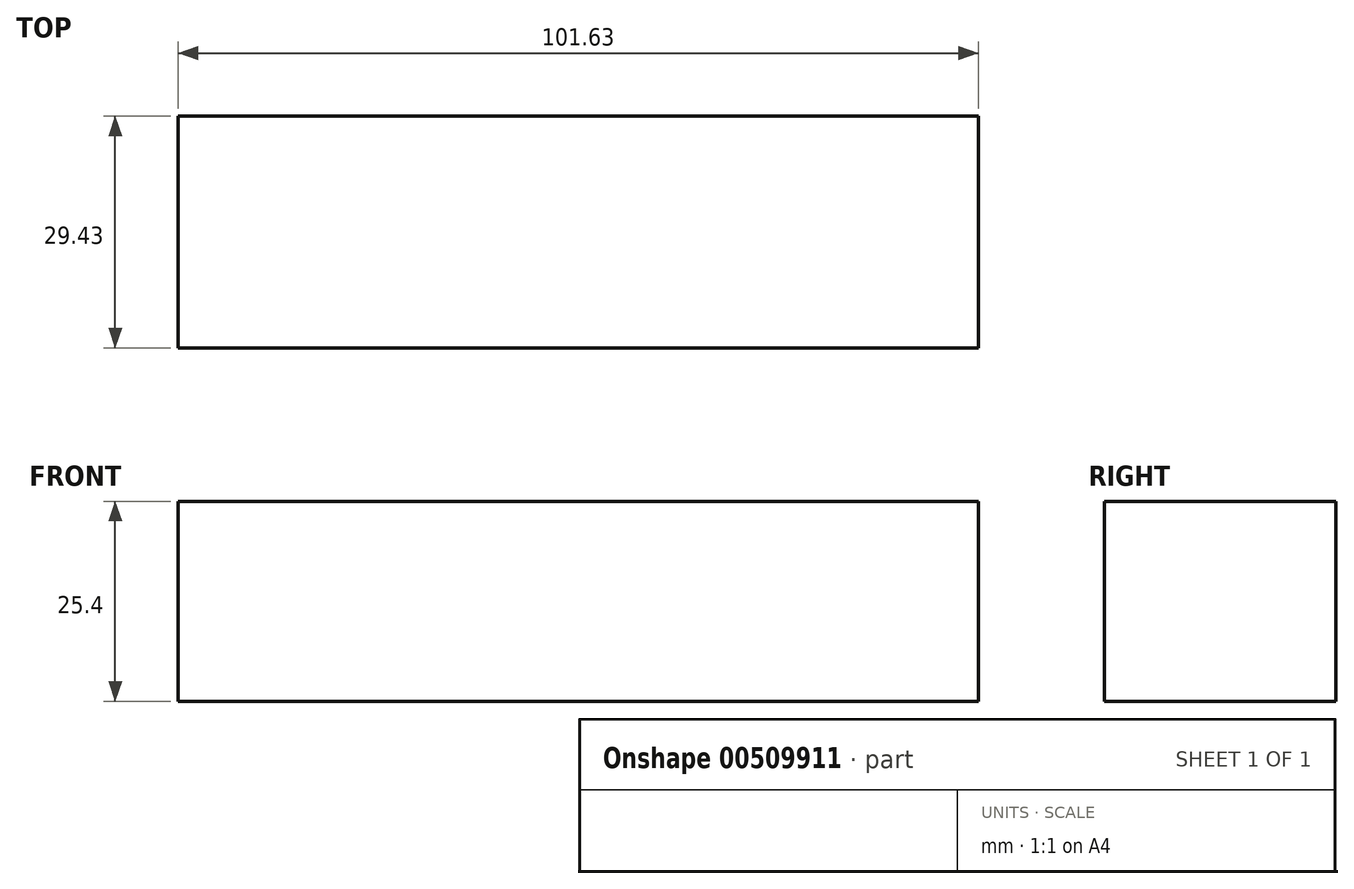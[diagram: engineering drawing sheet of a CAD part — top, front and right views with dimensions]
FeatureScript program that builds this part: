
annotation { "Feature Type Name" : "Feature", "Feature Type Description" : "" }
export const myFeature = defineFeature(function(context is Context, id is Id, definition is map)
    precondition{}
    {
        {
            var Q0;
            Q0=qCreatedBy(makeId("Top.planeOp"),FACE);
            var sketch = newSketch(context, id + "F0", { "sketchPlane" : qUnion([Q0])});
            skLineSegment(sketch, "E0.bottom", {"start": v(-6.42, -29.43) * mm, "end": v(95.21, -29.43) * mm});
            skLineSegment(sketch, "E0.top", {"start": v(-6.42, 0) * mm, "end": v(95.21, 0) * mm});
            skLineSegment(sketch, "E0.left", {"start": v(-6.42, -29.43) * mm, "end": v(-6.42, 0) * mm});
            skLineSegment(sketch, "E0.right", {"start": v(95.21, -29.43) * mm, "end": v(95.21, 0) * mm});
            skSolve(sketch);
        }
        {
            var Q0;
            Q0=makeQuery(id+"F0.imprint","IMPRINT",FACE,{"disambiguationData":[TD([[makeQuery(id+"F0.imprint","IMPRINT",EDGE,{"derivedFrom":sQuery(id+"F0.wireOp",EDGE,"E0.bottom")}),1.0]])]});
            extrude(context, id + "F1", {"entities" : qUnion([Q0]), "depth" : 25.4 * mm});
        }
    });
